# Revit family: P200921MX-008c_MEC8830H_B
name_source: partatom
category: Specialty Equipment
units: mm (PartAtom-declared; Revit-internal decimal feet)

## family parameters
Always vertical = Yes
Cut with Voids When Loaded = No
Enable Cutting in Views = No
Maintain Annotation Orientation = No
Part Type = Normal
Room Calculation Point = No
Round Connector Dimension = Use Diameter
Shared = No
Work Plane-Based = No

## types (1)
- MEC8830HB
    Accent Material = ARCAT - Plastic - White
    Amps = 0 A
    Body Material = ARCAT - Metal - Steel - Stainless
    Cooking Grate Material = ARCAT - Metal - Cast Iron 1/4" Plate
    Cooktop Material = ARCAT - Glass - Tempered - Black
    Default Elevation = 0"
    Depth = 22 7/8"
    Description = 30-Inch Electric Cooktop with Reversible Grill and Griddle
Table de cuisson électrique avec grille et plaque chauffante réversibles, 30 po
    Family Name = Cooking
    Feature 1 = Maytag® Exclusive Electric Cooktop with Reversible Grill and Griddle
Table de cuisson électrique Maytag® exclusive avec gril et plaque chauffante réversible
    Feature 2 = Reversible Grill and Griddle
Gril et plaque chauffante réversibles
    Feature 3 = 10/6-inch Dual-Choice™ Element
Élément Dual-Choice™ de 10/6 po
    Height = 5 1/4"
    Installation-Fabrication = https://www.whirlpool.com
https://www.whirlpool.com
    Knob Material = ARCAT - Metal - Cast Iron 1/4" Plate
    Manufacturer = Maytag
    Model = MEC8830HB
    No Border = Yes
    Side Border = No
    Voltage = 0 V
    Width = 30 13/16"

## geometry (parser evidence)
native form markers: Sweep x4
no freeform markers — native parametric forms only
